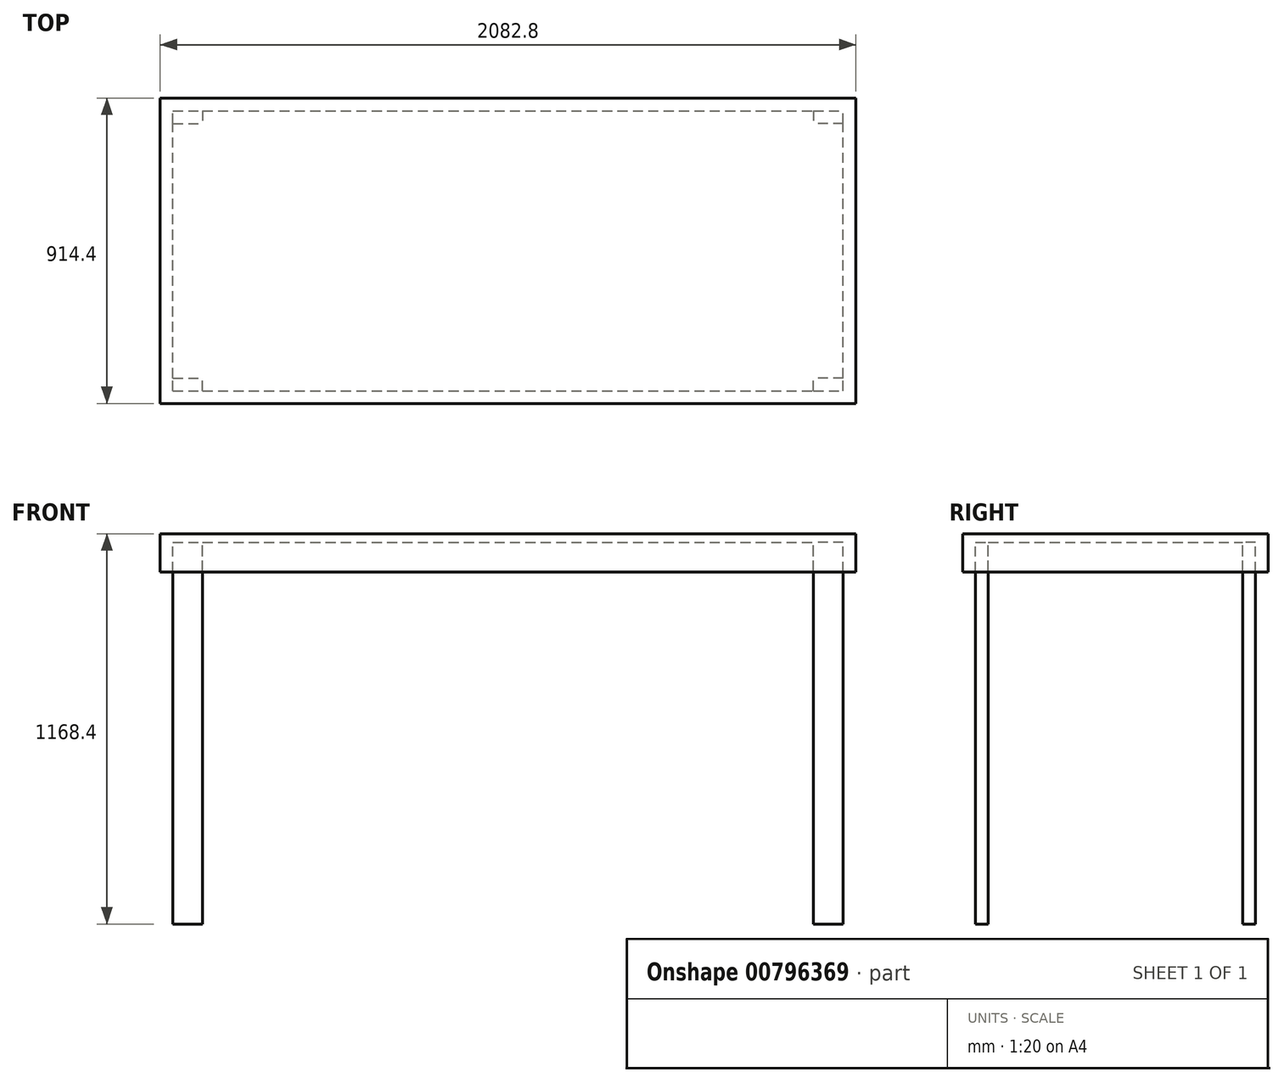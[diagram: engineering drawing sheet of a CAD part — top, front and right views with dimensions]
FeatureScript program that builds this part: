
annotation { "Feature Type Name" : "Feature", "Feature Type Description" : "" }
export const myFeature = defineFeature(function(context is Context, id is Id, definition is map)
    precondition{}
    {
        {
            var Q0;
            Q0=qCreatedBy(makeId("Top.planeOp"),FACE);
            var sketch = newSketch(context, id + "F0", { "sketchPlane" : qUnion([Q0])});
            skLineSegment(sketch, "E0.bottom", {"start": v(0, 0) * mm, "end": v(2082.8, 0) * mm});
            skLineSegment(sketch, "E0.top", {"start": v(0, -914.4) * mm, "end": v(2082.8, -914.4) * mm});
            skLineSegment(sketch, "E0.left", {"start": v(0, 0) * mm, "end": v(0, -914.4) * mm});
            skLineSegment(sketch, "E0.right", {"start": v(2082.8, 0) * mm, "end": v(2082.8, -914.4) * mm});
            skSolve(sketch);
        }
        {
            var Q0;
            Q0=makeQuery(id+"F0.imprint","IMPRINT",FACE,{"disambiguationData":[TD([[makeQuery(id+"F0.imprint","IMPRINT",EDGE,{"derivedFrom":sQuery(id+"F0.wireOp",EDGE,"E0.bottom")}),-1.0]])]});
            extrude(context, id + "F1", {"entities" : qUnion([Q0]), "depth" : 25.4 * mm, "offsetDistance" : 25.4 * mm});
        }
        {
            var Q0;
            Q0=makeQuery(id+"F1.opExtrude","SWEPT_FACE",FACE,{"disambiguationData":[OSD([sQuery(id+"F0.wireOp",EDGE,"E0.right")])]});
            var sketch = newSketch(context, id + "F2", { "sketchPlane" : qUnion([Q0])});
            skLineSegment(sketch, "E1", {"start": v(-914.4, 0) * mm, "end": v(-876.3, 0) * mm});
            skLineSegment(sketch, "E2", {"start": v(-876.3, 0) * mm, "end": v(-876.3, -88.9) * mm});
            skLineSegment(sketch, "E3", {"start": v(-876.3, -88.9) * mm, "end": v(-914.4, -88.9) * mm});
            skLineSegment(sketch, "E4", {"start": v(-914.4, -88.9) * mm, "end": v(-914.4, 0) * mm});
            skLineSegment(sketch, "E5.bottom", {"start": v(0, 0) * mm, "end": v(-38.1, 0) * mm});
            skLineSegment(sketch, "E5.top", {"start": v(0, -88.9) * mm, "end": v(-38.1, -88.9) * mm});
            skLineSegment(sketch, "E5.left", {"start": v(0, 0) * mm, "end": v(0, -88.9) * mm});
            skLineSegment(sketch, "E5.right", {"start": v(-38.1, 0) * mm, "end": v(-38.1, -88.9) * mm});
            skSolve(sketch);
        }
        {
            var Q0;
            Q0=makeQuery(id+"F2.imprint","IMPRINT",FACE,{"disambiguationData":[TD([[makeQuery(id+"F2.imprint","IMPRINT",EDGE,{"derivedFrom":sQuery(id+"F2.wireOp",EDGE,"E1")}),1.0]])]});
            var Q1;
            Q1=makeQuery(id+"F2.imprint","IMPRINT",FACE,{"disambiguationData":[TD([[makeQuery(id+"F2.imprint","IMPRINT",EDGE,{"derivedFrom":sQuery(id+"F2.wireOp",EDGE,"E5.bottom")}),1.0]])]});
            var Q2;
            Q2=makeQuery(id+"F1.opExtrude","SWEPT_FACE",FACE,{"disambiguationData":[OSD([sQuery(id+"F0.wireOp",EDGE,"E0.left")])]});
            extrude(context, id + "F3", {"entities" : qUnion([Q0, Q1]), "operationType" : NewBodyOperationType.ADD, "endBound" : BoundingType.UP_TO_SURFACE, "oppositeDirection" : true, "depth" : 2438.4 * mm, "endBoundEntityFace" : qUnion([Q2]), "offsetDistance" : 25.4 * mm});
        }
        {
            var Q0;
            Q0=makeQuery(id+"F3.opExtrude","SWEPT_FACE",FACE,{"disambiguationData":[OSD([sQuery(id+"F2.wireOp",EDGE,"E5.right")])]});
            var sketch = newSketch(context, id + "F4", { "sketchPlane" : qUnion([Q0])});
            skLineSegment(sketch, "E6.bottom", {"start": v(2082.8, 0) * mm, "end": v(2044.7, 0) * mm});
            skLineSegment(sketch, "E6.top", {"start": v(2082.8, -88.9) * mm, "end": v(2044.7, -88.9) * mm});
            skLineSegment(sketch, "E6.left", {"start": v(2082.8, 0) * mm, "end": v(2082.8, -88.9) * mm});
            skLineSegment(sketch, "E6.right", {"start": v(2044.7, 0) * mm, "end": v(2044.7, -88.9) * mm});
            skLineSegment(sketch, "E7.bottom", {"start": v(0, 0) * mm, "end": v(38.1, 0) * mm});
            skLineSegment(sketch, "E7.top", {"start": v(0, -88.9) * mm, "end": v(38.1, -88.9) * mm});
            skLineSegment(sketch, "E7.left", {"start": v(0, 0) * mm, "end": v(0, -88.9) * mm});
            skLineSegment(sketch, "E7.right", {"start": v(38.1, 0) * mm, "end": v(38.1, -88.9) * mm});
            skSolve(sketch);
        }
        {
            var Q0;
            Q0=makeQuery(id+"F4.imprint","IMPRINT",FACE,{"disambiguationData":[TD([[makeQuery(id+"F4.imprint","IMPRINT",EDGE,{"derivedFrom":sQuery(id+"F4.wireOp",EDGE,"E7.bottom")}),-1.0]])]});
            var Q1;
            Q1=makeQuery(id+"F4.imprint","IMPRINT",FACE,{"disambiguationData":[TD([[makeQuery(id+"F4.imprint","IMPRINT",EDGE,{"derivedFrom":sQuery(id+"F4.wireOp",EDGE,"E6.bottom")}),-1.0]])]});
            extrude(context, id + "F5", {"entities" : qUnion([Q0, Q1]), "operationType" : NewBodyOperationType.ADD, "endBound" : BoundingType.UP_TO_NEXT, "depth" : 25.4 * mm, "offsetDistance" : 25.4 * mm});
        }
        {
            var Q0;
            Q0=makeQuery(id+"F1.opExtrude","CAP_FACE",FACE,{"disambiguationData":[OSD([sQuery(id+"F0.wireOp",EDGE,"E0.bottom"),sQuery(id+"F0.wireOp",EDGE,"E0.top"),sQuery(id+"F0.wireOp",EDGE,"E0.left"),sQuery(id+"F0.wireOp",EDGE,"E0.right")])],"isStart":true});
            var sketch = newSketch(context, id + "F6", { "sketchPlane" : qUnion([Q0])});
            skLineSegment(sketch, "E8.bottom", {"start": v(38.1, 876.3) * mm, "end": v(127, 876.3) * mm});
            skLineSegment(sketch, "E8.top", {"start": v(38.1, 838.2) * mm, "end": v(127, 838.2) * mm});
            skLineSegment(sketch, "E8.left", {"start": v(38.1, 876.3) * mm, "end": v(38.1, 838.2) * mm});
            skLineSegment(sketch, "E8.right", {"start": v(127, 876.3) * mm, "end": v(127, 838.2) * mm});
            skLineSegment(sketch, "E9.bottom", {"start": v(2044.7, 876.3) * mm, "end": v(1955.8, 876.3) * mm});
            skLineSegment(sketch, "E9.top", {"start": v(2044.7, 838.2) * mm, "end": v(1955.8, 838.2) * mm});
            skLineSegment(sketch, "E9.left", {"start": v(2044.7, 876.3) * mm, "end": v(2044.7, 838.2) * mm});
            skLineSegment(sketch, "E9.right", {"start": v(1955.8, 876.3) * mm, "end": v(1955.8, 838.2) * mm});
            skLineSegment(sketch, "E10.bottom", {"start": v(2044.7, 38.1) * mm, "end": v(1955.8, 38.1) * mm});
            skLineSegment(sketch, "E10.top", {"start": v(2044.7, 76.2) * mm, "end": v(1955.8, 76.2) * mm});
            skLineSegment(sketch, "E10.left", {"start": v(2044.7, 38.1) * mm, "end": v(2044.7, 76.2) * mm});
            skLineSegment(sketch, "E10.right", {"start": v(1955.8, 38.1) * mm, "end": v(1955.8, 76.2) * mm});
            skLineSegment(sketch, "E11.bottom", {"start": v(38.1, 38.1) * mm, "end": v(127, 38.1) * mm});
            skLineSegment(sketch, "E11.top", {"start": v(38.1, 76.2) * mm, "end": v(127, 76.2) * mm});
            skLineSegment(sketch, "E11.left", {"start": v(38.1, 38.1) * mm, "end": v(38.1, 76.2) * mm});
            skLineSegment(sketch, "E11.right", {"start": v(127, 38.1) * mm, "end": v(127, 76.2) * mm});
            skSolve(sketch);
        }
        {
            var Q0;
            Q0=makeQuery(id+"F6.imprint","IMPRINT",FACE,{"disambiguationData":[TD([[makeQuery(id+"F6.imprint","IMPRINT",EDGE,{"derivedFrom":sQuery(id+"F6.wireOp",EDGE,"784e618c-9e80-4dcf-ae9d-e2e26c954d36.1.0.0")}),-1.0]])]});
            var Q1;
            Q1=makeQuery(id+"F6.imprint","IMPRINT",FACE,{"disambiguationData":[TD([[makeQuery(id+"F6.imprint","IMPRINT",EDGE,{"derivedFrom":sQuery(id+"F6.wireOp",EDGE,"784e618c-9e80-4dcf-ae9d-e2e26c954d36.0.1.0")}),-1.0]])]});
            var Q2;
            Q2=makeQuery(id+"F6.imprint","IMPRINT",FACE,{"disambiguationData":[TD([[makeQuery(id+"F6.imprint","IMPRINT",EDGE,{"derivedFrom":sQuery(id+"F6.wireOp",EDGE,"784e618c-9e80-4dcf-ae9d-e2e26c954d36.1.1.0")}),-1.0]])]});
            var Q3;
            Q3=makeQuery(id+"F6.imprint","IMPRINT",FACE,{"disambiguationData":[TD([[makeQuery(id+"F6.imprint","IMPRINT",EDGE,{"derivedFrom":sQuery(id+"F6.wireOp",EDGE,"E8.bottom")}),-1.0]])]});
            var Q4;
            Q4=makeQuery(id+"F6.imprint","IMPRINT",FACE,{"disambiguationData":[TD([[makeQuery(id+"F6.imprint","IMPRINT",EDGE,{"derivedFrom":sQuery(id+"F6.wireOp",EDGE,"E11.bottom")}),1.0]])]});
            var Q5;
            Q5=makeQuery(id+"F6.imprint","IMPRINT",FACE,{"disambiguationData":[TD([[makeQuery(id+"F6.imprint","IMPRINT",EDGE,{"derivedFrom":sQuery(id+"F6.wireOp",EDGE,"E10.bottom")}),1.0]])]});
            var Q6;
            Q6=makeQuery(id+"F6.imprint","IMPRINT",FACE,{"disambiguationData":[TD([[makeQuery(id+"F6.imprint","IMPRINT",EDGE,{"derivedFrom":sQuery(id+"F6.wireOp",EDGE,"E9.bottom")}),-1.0]])]});
            extrude(context, id + "F7", {"entities" : qUnion([Q0, Q1, Q2, Q3, Q4, Q5, Q6]), "operationType" : NewBodyOperationType.ADD, "depth" : 1143 * mm, "offsetDistance" : 25.4 * mm});
        }
    });
